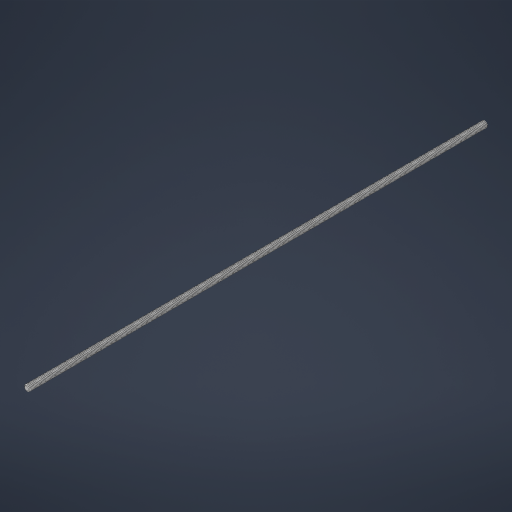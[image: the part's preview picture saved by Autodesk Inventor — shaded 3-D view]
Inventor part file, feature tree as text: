
AUTODESK INVENTOR PART (.ipt)
format: ipt  version: 2023 (Build 270158000, 158)  size: 6,530,560 bytes
history: native  units: in
note: dims shown in document units (in); Inventor stores cm internally (conversion verified against a paired STEP export)
features: mirror x1
ambient origin geometry x8: Origin, YZ Plane, XZ Plane, XY Plane, X Axis, Y Axis, Z Axis, Center Point
bodies: Solid1 (feature_tree)
feature tree (1):
  mirror  "Mirror1"
